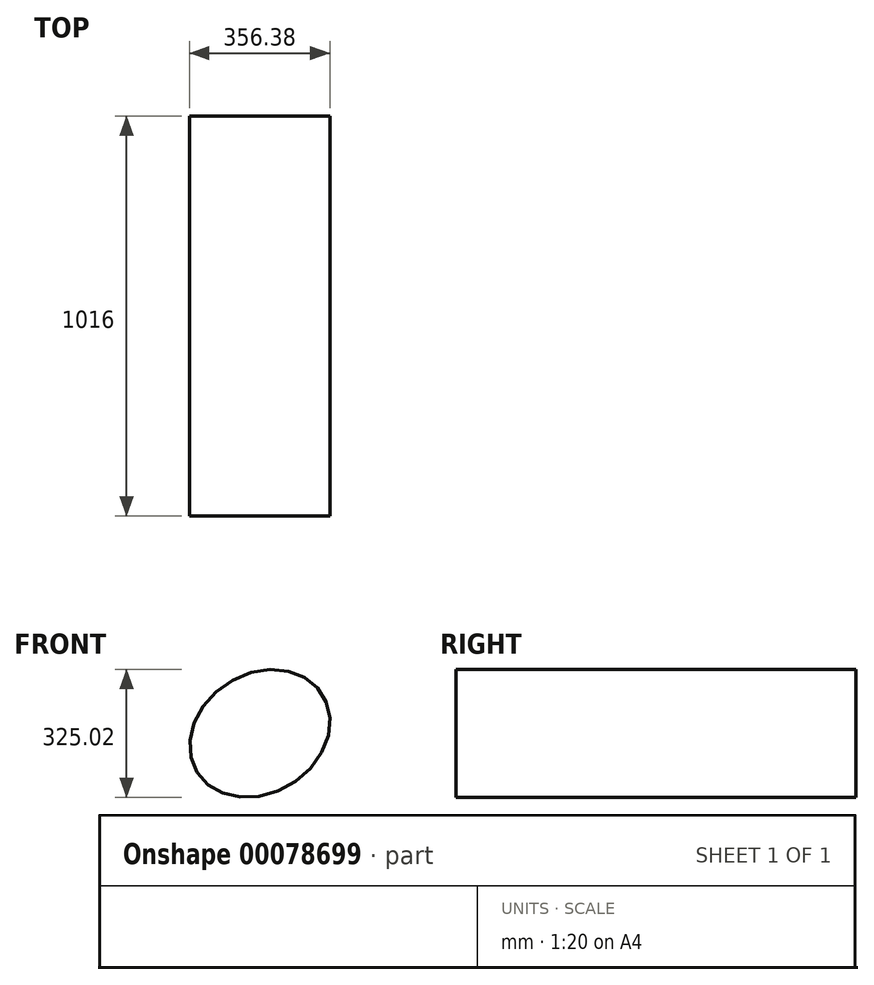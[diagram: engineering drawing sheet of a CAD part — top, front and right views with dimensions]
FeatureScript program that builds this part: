
annotation { "Feature Type Name" : "Feature", "Feature Type Description" : "" }
export const myFeature = defineFeature(function(context is Context, id is Id, definition is map)
    precondition{}
    {
        {
            var Q0;
            Q0=qCreatedBy(makeId("Front.planeOp"),FACE);
            var sketch = newSketch(context, id + "F0", { "sketchPlane" : qUnion([Q0])});
            skEllipse(sketch, "E0", {"center": v(-67.95, -47.17) * mm, "majorRadius": 151.76 * mm, "minorRadius": 187.43 * mm, "majorAxis": v(-0.53, 0.85)});
            skSolve(sketch);
        }
        {
            var Q0;
            Q0 = qSketchRegion(id + "F0", true);
            extrude(context, id + "F1", {"entities" : qUnion([Q0]), "depth" : 1016 * mm});
        }
    });
